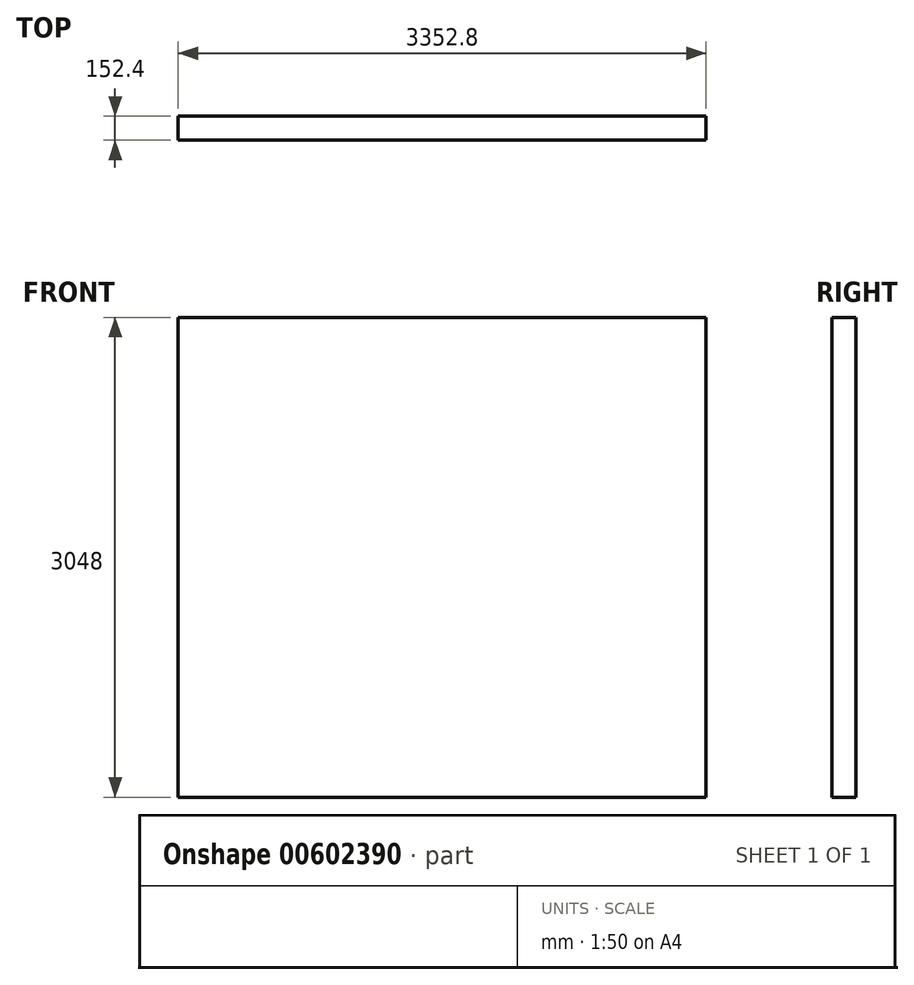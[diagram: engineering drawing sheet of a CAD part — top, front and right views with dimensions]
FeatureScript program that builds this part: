
annotation { "Feature Type Name" : "Feature", "Feature Type Description" : "" }
export const myFeature = defineFeature(function(context is Context, id is Id, definition is map)
    precondition{}
    {
        {
            var Q0;
            Q0=qCreatedBy(makeId("Front.planeOp"),FACE);
            var sketch = newSketch(context, id + "F0", { "sketchPlane" : qUnion([Q0])});
            skLineSegment(sketch, "E0.bottom", {"start": v(-1676.4, 1524) * mm, "end": v(1676.4, 1524) * mm});
            skLineSegment(sketch, "E0.top", {"start": v(-1676.4, -1524) * mm, "end": v(1676.4, -1524) * mm});
            skLineSegment(sketch, "E0.left", {"start": v(-1676.4, 1524) * mm, "end": v(-1676.4, -1524) * mm});
            skLineSegment(sketch, "E0.right", {"start": v(1676.4, 1524) * mm, "end": v(1676.4, -1524) * mm});
            skPoint(sketch, "E0.middle", {"position": v(0, 0) * mm});
            skSolve(sketch);
        }
        {
            var Q0;
            Q0=makeQuery(id+"F0.imprint","IMPRINT",FACE,{"disambiguationData":[TD([[makeQuery(id+"F0.imprint","IMPRINT",EDGE,{"derivedFrom":sQuery(id+"F0.wireOp",EDGE,"E0.bottom")}),-1.0]])]});
            extrude(context, id + "F1", {"entities" : qUnion([Q0]), "depth" : 152.4 * mm, "offsetDistance" : 30.48 * mm});
        }
    });
